# Revit family: Faucet-Lavatory-American_Standard-Monterrey-65401X5_Series
name_source: partatom
category: Plumbing Fixtures
units: mm (PartAtom-declared; Revit-internal decimal feet)

## family parameters
Always vertical = No
Cut with Voids When Loaded = No
OmniClass Number = 23.45.55.17
OmniClass Title = Mixing Faucets
Part Type = Normal
Room Calculation Point = No
Round Connector Dimension = Use Diameter
Shared = Yes
Work Plane-Based = Yes

## types (2) — shared parameters
ADA Compliant = Yes
Assembly Code = D2020300
CEC Compliant = Yes
CW Connection = Yes
CWFU = 1.5
CalGreen Compliant = Yes
Cold Water Connection Diameter = 1/2"
Cold Water Connection Radius = 1/4"
Cold Water Connection Width = 4"
Default Elevation = 0"
Description = Monterrey® 8-Inch Widespread Gooseneck Faucet With Lever Handles 0.5 gpm/1.9 Lpm
Finish = Brass-American Standard-002-Polished Chrome
Flow Rate = 0.5 gpm/1.9 Lpm
HW Connection = Yes
HWFU = 1.5
Height = 10 5/8"
Hot Water Connection Diameter = 1"
Hot Water Connection Radius = 1/4"
Hot Water Connection Width = 4"
IAPMO Compliance = Vandal Resistance, ANSI 117.1, ASME A112.18.1, CSA B125.1, NSF 372
Installation Type = Deck Mounted
Length = 5"
Manufacturer = American Standard
Material = Brass-American Standard-002-Polished Chrome
Price = Prices may vary. Please consult Manufacturer Representative for most up-to-date price list.
Product Documentation Link = https://americanstandard.box.com
Product Page URL = https://www.americanstandard-us.com
URL = http://www.americanstandard-us.com
Vent Connection = No
Warranty Information = 5 Year Limited Warranty for Commercial Installations
Waste Connection = No
Width = 15 3/4"
zero-valued in all types: WFU

## per-type parameters (varying)
| type | Faucets Width | Lever Handle | Wrist Blade Handles |
| 6540175.002 | 3 7/8" | No | Yes |
| 6540145.002 | 2 1/4" | Yes | No |

note: column(s) folded — value = type name in every type: Model

## geometry (parser evidence)
native form markers: Sweep x2
no freeform markers — native parametric forms only
